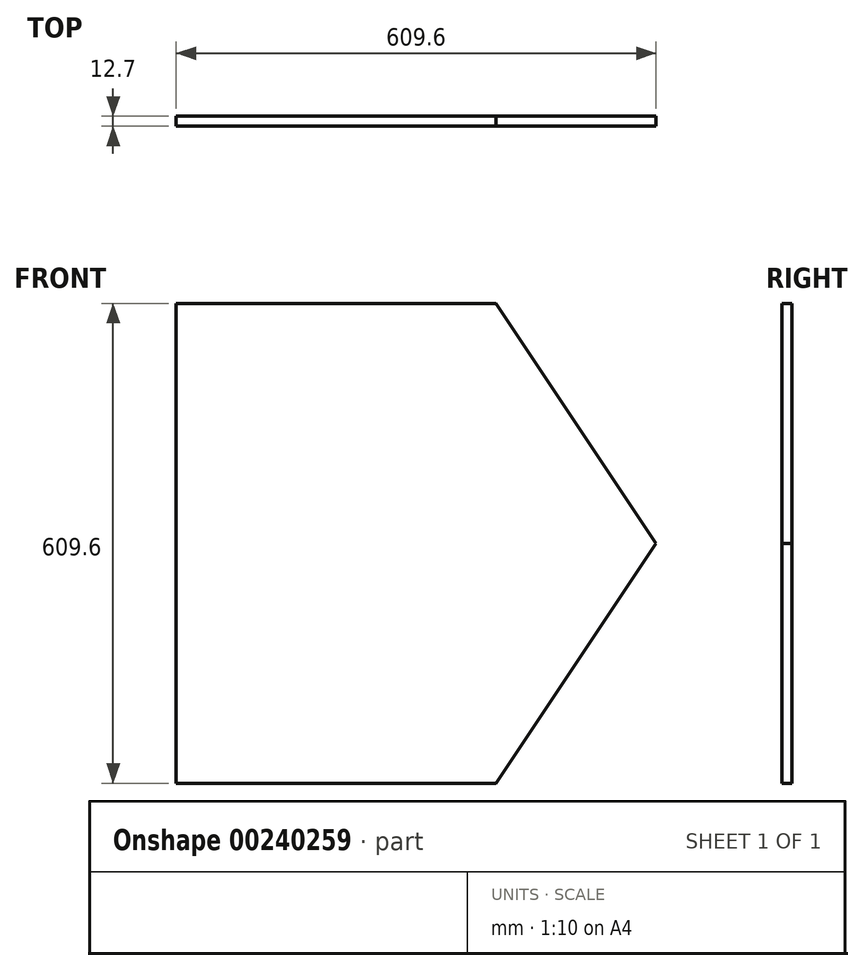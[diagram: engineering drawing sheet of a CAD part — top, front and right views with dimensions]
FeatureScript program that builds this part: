
annotation { "Feature Type Name" : "Feature", "Feature Type Description" : "" }
export const myFeature = defineFeature(function(context is Context, id is Id, definition is map)
    precondition{}
    {
        {
            var Q0;
            Q0=qCreatedBy(makeId("Front.planeOp"),FACE);
            var sketch = newSketch(context, id + "F0", { "sketchPlane" : qUnion([Q0])});
            skLineSegment(sketch, "E0", {"start": v(0, 0) * mm, "end": v(406.4, 0) * mm});
            skLineSegment(sketch, "E1", {"start": v(406.4, 0) * mm, "end": v(609.6, 304.8) * mm});
            skLineSegment(sketch, "E2", {"start": v(0, 609.6) * mm, "end": v(0, 0) * mm});
            skLineSegment(sketch, "E3", {"start": v(0, 609.6) * mm, "end": v(406.4, 609.6) * mm});
            skLineSegment(sketch, "E4", {"start": v(406.4, 609.6) * mm, "end": v(609.6, 304.8) * mm});
            skPoint(sketch, "E5.orphan", {"position": v(0, 769.7) * mm});
            skSolve(sketch);
        }
        {
            var Q0;
            Q0 = qSketchRegion(id + "F0", true);
            extrude(context, id + "F1", {"entities" : qUnion([Q0]), "oppositeDirection" : true, "depth" : 12.7 * mm});
        }
    });
